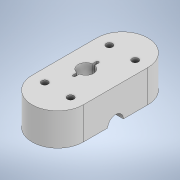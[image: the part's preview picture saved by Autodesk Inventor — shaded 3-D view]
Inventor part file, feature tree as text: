
AUTODESK INVENTOR PART (.ipt)
format: ipt  version: 2020 (Build 240168000, 168)  size: 203,776 bytes
history: native  units: mm
features: fillet x3, sketch x3, extrude x2, hole x1
ambient origin geometry x8: Origin, YZ Plane, XZ Plane, XY Plane, X Axis, Y Axis, Z Axis, Center Point
bodies: Solid1 (feature_tree)
feature tree (9):
  extrude  "Extrusion1"  Depth=39.6mm
  extrude  "Extrusion2"  Depth=1.0mm
  fillet  "Fillet1"  Radius=10.0mm
  fillet  "Fillet2"  Radius=2.0mm
  fillet  "Fillet3"  Radius=20.0mm
  hole  "Hole1"  [1 undecoded]
  sketch  "Sketch1"  dims[d7=12.05mm d10=39.6mm]
  sketch  "Sketch2"  dims[d11=39.6mm d12=1.0mm d13=10.0mm d14=2.0mm d15=20.0mm]
  sketch  "Sketch4"  dims[d16=25.0mm d17=0.0mm d18=6.0mm d19=0.0mm d20=6.0mm d21=6.0mm d22=1.0mm d30=10.0mm d31=1.0mm d32=20.0mm d33=50.0mm d34=5.0mm d35=6.0mm d36=8.4mm d37=5.0mm d38=90.0deg d39=8.0mm d40=20.594885mm]
note: 1 required parameter value undecoded (feature->parameter linkage not recoverable at this tier; creation-order binding heuristic only, values carry confidence <= 0.55)
